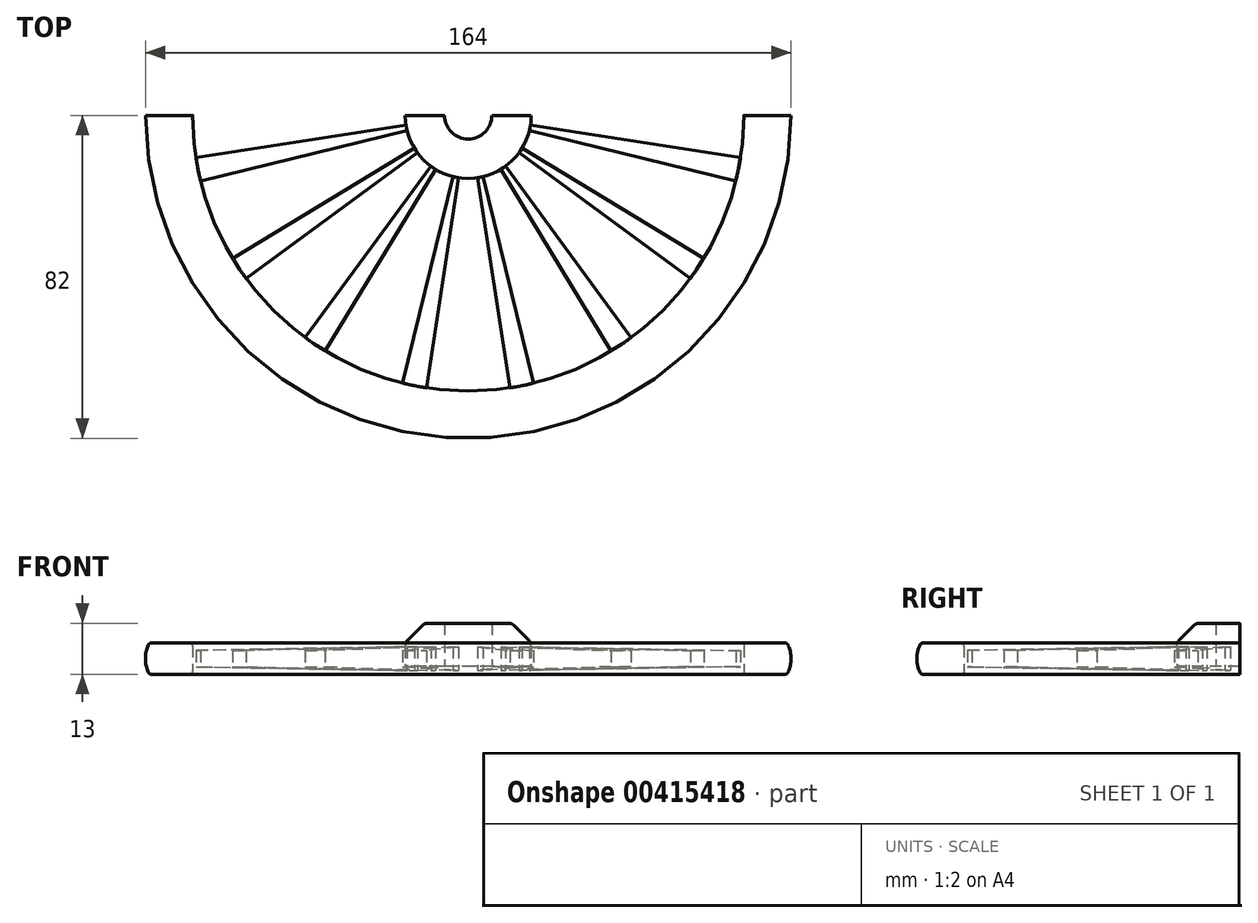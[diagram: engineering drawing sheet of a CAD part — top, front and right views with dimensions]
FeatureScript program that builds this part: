
annotation { "Feature Type Name" : "Feature", "Feature Type Description" : "" }
export const myFeature = defineFeature(function(context is Context, id is Id, definition is map)
    precondition{}
    {
        {
            var Q0;
            Q0=qCreatedBy(makeId("Front.planeOp"),FACE);
            var sketch = newSketch(context, id + "F0", { "sketchPlane" : qUnion([Q0])});
            skLineSegment(sketch, "E0", {"start": v(-2, 0) * mm, "end": v(-2, 13) * mm});
            skLineSegment(sketch, "E1", {"start": v(-2, 13) * mm, "end": v(-10.24, 13) * mm});
            skLineSegment(sketch, "E2", {"start": v(-16, 7.24) * mm, "end": v(-16, 0) * mm});
            skLineSegment(sketch, "E3", {"start": v(-16, 0) * mm, "end": v(-2, 0) * mm});
            skLineSegment(sketch, "E4", {"start": v(-15.4, 8.66) * mm, "end": v(-11.65, 12.41) * mm});
            skPoint(sketch, "E5.visualSharp", {"position": v(-11.07, 13) * mm});
            skArc(sketch, "E5.filletArc", {"start": v(-10.24, 13) * mm, "mid": v(-11, 12.85) * mm, "end": v(-11.65, 12.41) * mm});
            skPoint(sketch, "E6.visualSharp", {"position": v(-16, 8.07) * mm});
            skArc(sketch, "E6.filletArc", {"start": v(-15.4, 8.66) * mm, "mid": v(-15.84, 8) * mm, "end": v(-16, 7.24) * mm});
            skSolve(sketch);
        }
        {
            var Q0;
            Q0=qCreatedBy(makeId("Front.planeOp"),FACE);
            var sketch = newSketch(context, id + "F1", { "sketchPlane" : qUnion([Q0])});
            skLineSegment(sketch, "E7", {"start": v(0, 0) * mm, "end": v(0, 15.4) * mm, "construction": true});
            skSolve(sketch);
        }
        {
            var Q0;
            Q0=qSketchRegion(id+"F0",true);
            var Q1;
            Q1=sQuery(id+"F1.wireOp",EDGE,"E7");
            revolve(context, id + "F2", {"entities" : qUnion([Q0]), "axis" : qUnion([Q1]), "revolveType" : RevolveType.ONE_DIRECTION, "angle" : 180 * degree});
        }
        {
            var Q0;
            Q0=qCreatedBy(makeId("Front.planeOp"),FACE);
            var sketch = newSketch(context, id + "F3", { "sketchPlane" : qUnion([Q0])});
            skLineSegment(sketch, "E8", {"start": v(-70.8, 0) * mm, "end": v(-80.37, 0) * mm});
            skLineSegment(sketch, "E9", {"start": v(-82, 0) * mm, "end": v(-82, 8) * mm, "construction": true});
            skLineSegment(sketch, "E10", {"start": v(-80.37, 8) * mm, "end": v(-70.75, 8) * mm});
            skLineSegment(sketch, "E11", {"start": v(-70, 7.25) * mm, "end": v(-70, 0.8) * mm});
            skLineSegment(sketch, "E12", {"start": v(-81, 8) * mm, "end": v(-81, 0) * mm, "construction": true});
            skArc(sketch, "E13", {"start": v(-81.3, 7.4) * mm, "mid": v(-82, 4) * mm, "end": v(-81.3, 0.6) * mm});
            skPoint(sketch, "E14.visualSharp", {"position": v(-81, 8) * mm});
            skArc(sketch, "E14.filletArc", {"start": v(-80.37, 8) * mm, "mid": v(-80.92, 7.84) * mm, "end": v(-81.3, 7.4) * mm});
            skPoint(sketch, "E15.visualSharp", {"position": v(-81, 0) * mm});
            skArc(sketch, "E15.filletArc", {"start": v(-81.3, 0.6) * mm, "mid": v(-80.92, 0.16) * mm, "end": v(-80.37, 0) * mm});
            skPoint(sketch, "E16.visualSharp", {"position": v(-70, 8) * mm});
            skArc(sketch, "E16.filletArc", {"start": v(-70, 7.25) * mm, "mid": v(-70.22, 7.78) * mm, "end": v(-70.75, 8) * mm});
            skPoint(sketch, "E17.visualSharp", {"position": v(-70, 0) * mm});
            skArc(sketch, "E17.filletArc", {"start": v(-70.8, 0) * mm, "mid": v(-70.23, 0.23) * mm, "end": v(-70, 0.8) * mm});
            skSolve(sketch);
        }
        {
            var Q0;
            Q0=qSketchRegion(id+"F3",true);
            var Q1;
            Q1=sQuery(id+"F1.wireOp",EDGE,"E7");
            revolve(context, id + "F4", {"entities" : qUnion([Q0]), "axis" : qUnion([Q1]), "revolveType" : RevolveType.ONE_DIRECTION, "angle" : 180 * degree});
        }
        {
            var Q0;
            Q0=sQuery(id+"F1.wireOp",EDGE,"E7");
            var Q1;
            Q1=qCreatedBy(makeId("Front.planeOp"),FACE);
            cPlane(context, id + "F5", {"entities" : qUnion([Q0, Q1]), "cplaneType" : CPlaneType.LINE_ANGLE, "offset" : 25 * mm, "angle" : 11.25 * degree, "width" : 150 * mm, "height" : 150 * mm});
        }
        {
            var Q0;
            Q0=qCreatedBy(makeId("Top.planeOp"),FACE);
            cPlane(context, id + "F6", {"entities" : qUnion([Q0]), "cplaneType" : CPlaneType.OFFSET, "offset" : 1 * mm, "width" : 150 * mm, "height" : 150 * mm});
        }
        {
            var Q0;
            Q0=qCreatedBy(id+"F6.planeOp",FACE);
            var sketch = newSketch(context, id + "F7", { "sketchPlane" : qUnion([Q0])});
            skLineSegment(sketch, "E18", {"start": v(0, 0) * mm, "end": v(-68.65, -13.66) * mm, "construction": true});
            skLineSegment(sketch, "E19", {"start": v(0, 0) * mm, "end": v(-15.8, -2.43) * mm, "construction": true});
            skLineSegment(sketch, "E20", {"start": v(0, 0) * mm, "end": v(-15.54, -3.8) * mm, "construction": true});
            skLineSegment(sketch, "E21", {"start": v(-15.54, -3.8) * mm, "end": v(-15.54, -3.8) * mm});
            skPoint(sketch, "E22.orphan", {"position": v(-16, 0) * mm});
            skPoint(sketch, "E23.0.start.orphan", {"position": v(16, 0) * mm});
            skLineSegment(sketch, "E24", {"start": v(-15.8, -2.43) * mm, "end": v(-69.19, -10.65) * mm});
            skArc(sketch, "E25", {"start": v(-15.54, -3.8) * mm, "mid": v(-15.69, -3.12) * mm, "end": v(-15.8, -2.43) * mm});
            skLineSegment(sketch, "E26", {"start": v(-15.54, -3.8) * mm, "end": v(-68, -16.64) * mm});
            skArc(sketch, "E27.0", {"start": v(-68, -16.64) * mm, "mid": v(-68.65, -13.66) * mm, "end": v(-69.19, -10.65) * mm});
            skPoint(sketch, "E28.orphan", {"position": v(-70, 0) * mm});
            skPoint(sketch, "E29.orphan", {"position": v(70, 0) * mm});
            skSolve(sketch);
        }
        {
            var Q0;
            Q0=qSketchRegion(id+"F7",true);
            extrude(context, id + "F8", {"entities" : qUnion([Q0]), "depth" : 6 * mm});
        }
        {
            var Q0;
            Q0=makeQuery(id+"F8.opExtrude","SWEPT_BODY",BODY,{"disambiguationData":[OSD([sQuery(id+"F7.wireOp",EDGE,"E24"),sQuery(id+"F7.wireOp",EDGE,"E25"),sQuery(id+"F7.wireOp",EDGE,"E26"),sQuery(id+"F7.wireOp",EDGE,"E27.0")])]});
            var Q1;
            Q1=sQuery(id+"F1.wireOp",EDGE,"E7");
            circularPattern(context, id + "F9", {"entities" : qUnion([Q0]), "axis" : qUnion([Q1]), "angle" : 157.5 * degree, "instanceCount" : 8, "equalSpace" : true});
        }
        {
            var Q0;
            Q0=qCreatedBy(makeId("Front.planeOp"),FACE);
            var sketch = newSketch(context, id + "F10", { "sketchPlane" : qUnion([Q0])});
            skLineSegment(sketch, "E30.0", {"start": v(-16, 7) * mm, "end": v(-70, 7) * mm});
            skPoint(sketch, "E31.orphan", {"position": v(-16, 7.24) * mm});
            skPoint(sketch, "E32.orphan", {"position": v(-15.8, 7) * mm});
            skLineSegment(sketch, "E33.0", {"start": v(-70, 7) * mm, "end": v(-70, 6.06) * mm});
            skPoint(sketch, "E34.orphan", {"position": v(-69.19, 7) * mm});
            skPoint(sketch, "E35.orphan", {"position": v(-70, 7.25) * mm});
            skLineSegment(sketch, "E36", {"start": v(-16, 7) * mm, "end": v(-70, 6.06) * mm});
            skPoint(sketch, "E37.orphan", {"position": v(-70, 0.8) * mm});
            skPoint(sketch, "E38.0.end.orphan", {"position": v(-16, 0) * mm});
            skSolve(sketch);
        }
        {
            var Q0;
            Q0=qSketchRegion(id+"F10",true);
            var Q1;
            Q1=sQuery(id+"F1.wireOp",EDGE,"E7");
            revolve(context, id + "F11", {"operationType" : NewBodyOperationType.REMOVE, "entities" : qUnion([Q0]), "axis" : qUnion([Q1]), "revolveType" : RevolveType.FULL, "oppositeDirection" : true});
        }
        {
            var Q0;
            Q0=qCreatedBy(makeId("Front.planeOp"),FACE);
            var sketch = newSketch(context, id + "F12", { "sketchPlane" : qUnion([Q0])});
            skLineSegment(sketch, "E39.0", {"start": v(-70, 1.94) * mm, "end": v(-70, 1) * mm});
            skLineSegment(sketch, "E40.0", {"start": v(-16, 1) * mm, "end": v(-70, 1) * mm});
            skPoint(sketch, "E41.orphan", {"position": v(-69.19, 1) * mm});
            skPoint(sketch, "E42.orphan", {"position": v(-70, 0.8) * mm});
            skPoint(sketch, "E43.orphan", {"position": v(-15.8, 1) * mm});
            skPoint(sketch, "E44.orphan", {"position": v(-16, 0) * mm});
            skLineSegment(sketch, "E45", {"start": v(-16, 1) * mm, "end": v(-70, 1.94) * mm});
            skPoint(sketch, "E46.orphan", {"position": v(-70, 7.25) * mm});
            skPoint(sketch, "E47.0.start.orphan", {"position": v(-16, 7.24) * mm});
            skSolve(sketch);
        }
        {
            var Q0;
            Q0=qSketchRegion(id+"F12",true);
            var Q1;
            Q1=sQuery(id+"F1.wireOp",EDGE,"E7");
            revolve(context, id + "F13", {"operationType" : NewBodyOperationType.REMOVE, "entities" : qUnion([Q0]), "axis" : qUnion([Q1]), "revolveType" : RevolveType.FULL, "oppositeDirection" : true});
        }
        {
            var Q0;
            Q0=qCreatedBy(makeId("Front.planeOp"),FACE);
            var sketch = newSketch(context, id + "F14", { "sketchPlane" : qUnion([Q0])});
            skLineSegment(sketch, "E48.0", {"start": v(2, 0) * mm, "end": v(2, 13) * mm});
            skLineSegment(sketch, "E49.0", {"start": v(2, 13) * mm, "end": v(6, 13) * mm});
            skLineSegment(sketch, "E50.0", {"start": v(16, 0) * mm, "end": v(2, 0) * mm});
            skLineSegment(sketch, "E51", {"start": v(6, 13) * mm, "end": v(6, 2) * mm});
            skPoint(sketch, "E52.orphan", {"position": v(10.24, 13) * mm});
            skPoint(sketch, "E53.orphan", {"position": v(16, 0) * mm});
            skLineSegment(sketch, "E54.0", {"start": v(16, 2) * mm, "end": v(16, 0) * mm});
            skLineSegment(sketch, "E55", {"start": v(16, 2) * mm, "end": v(6, 2) * mm});
            skPoint(sketch, "E56.orphan", {"position": v(16, 7.24) * mm});
            skSolve(sketch);
        }
        {
            var Q0;
            Q0=qSketchRegion(id+"F14",true);
            var Q1;
            Q1=sQuery(id+"F1.wireOp",EDGE,"E7");
            revolve(context, id + "F15", {"operationType" : NewBodyOperationType.REMOVE, "entities" : qUnion([Q0]), "axis" : qUnion([Q1]), "revolveType" : RevolveType.FULL});
        }
    });
